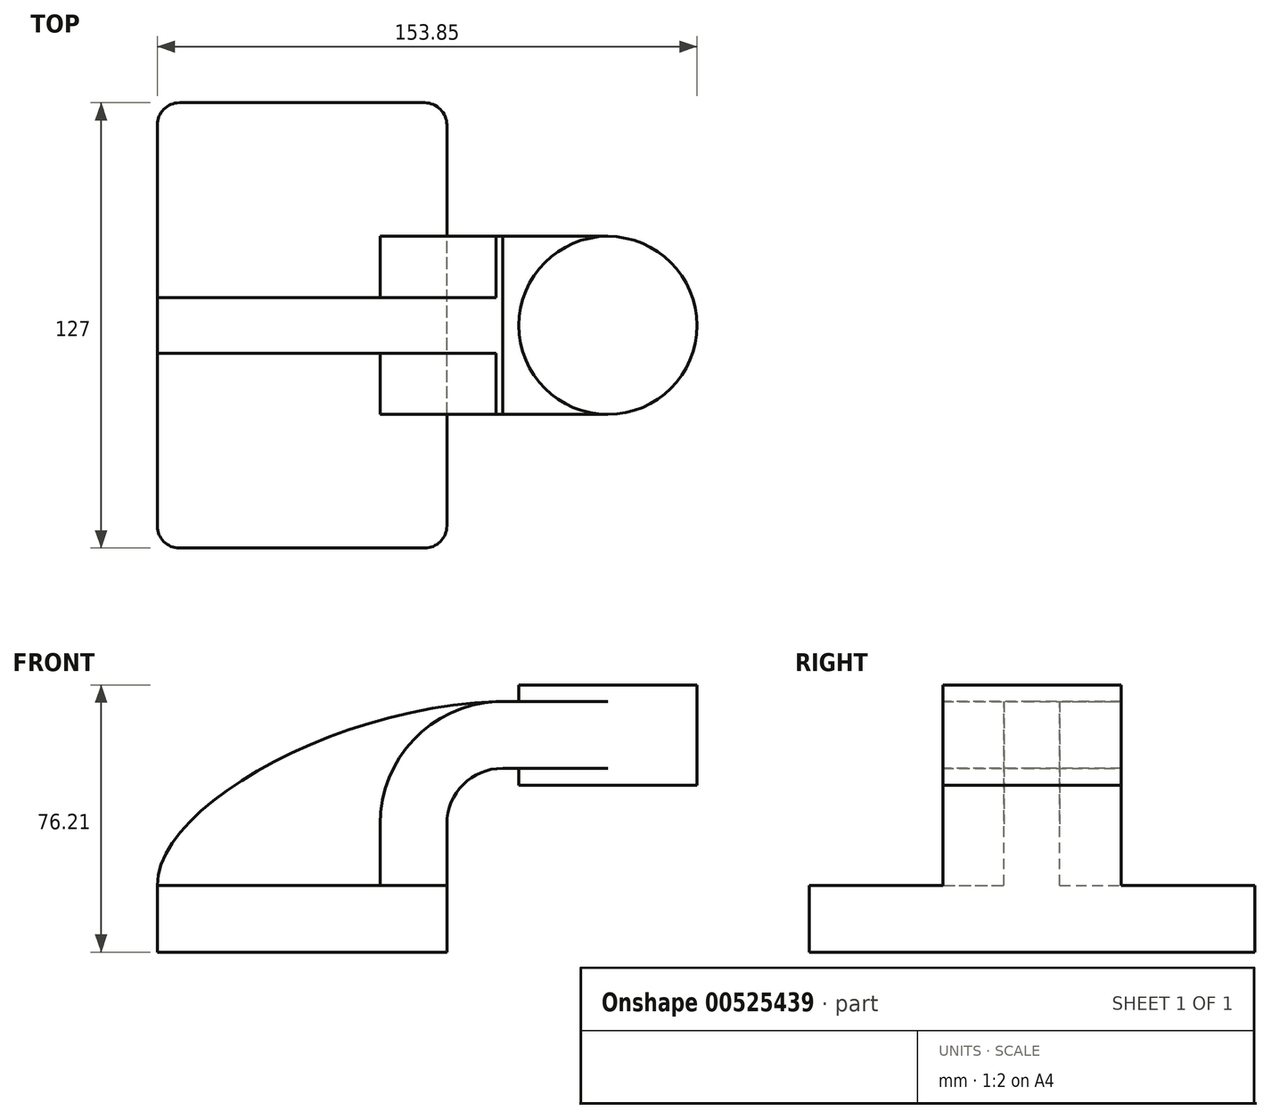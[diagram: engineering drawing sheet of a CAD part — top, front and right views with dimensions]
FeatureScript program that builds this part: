
annotation { "Feature Type Name" : "Feature", "Feature Type Description" : "" }
export const myFeature = defineFeature(function(context is Context, id is Id, definition is map)
    precondition{}
    {
        {
            var Q0;
            Q0=qCreatedBy(makeId("Front.planeOp"),FACE);
            var sketch = newSketch(context, id + "F0", { "sketchPlane" : qUnion([Q0])});
            skLineSegment(sketch, "E0.bottom", {"start": v(-41.28, 9.52) * mm, "end": v(41.27, 9.53) * mm});
            skLineSegment(sketch, "E0.top", {"start": v(-41.28, -9.53) * mm, "end": v(41.28, -9.53) * mm});
            skLineSegment(sketch, "E0.left", {"start": v(-41.28, 9.52) * mm, "end": v(-41.27, -9.53) * mm});
            skLineSegment(sketch, "E0.right", {"start": v(41.28, 9.53) * mm, "end": v(41.28, -9.52) * mm});
            skPoint(sketch, "E0.middle", {"position": v(0, 0) * mm});
            skLineSegment(sketch, "E1.bottom", {"start": v(112.57, 38.1) * mm, "end": v(61.77, 38.1) * mm});
            skLineSegment(sketch, "E1.top", {"start": v(112.57, 66.68) * mm, "end": v(61.77, 66.68) * mm});
            skLineSegment(sketch, "E1.left", {"start": v(112.57, 38.1) * mm, "end": v(112.57, 66.68) * mm});
            skLineSegment(sketch, "E1.right", {"start": v(61.77, 38.1) * mm, "end": v(61.77, 66.68) * mm});
            skPoint(sketch, "E1.middle", {"position": v(87.17, 52.39) * mm});
            skLineSegment(sketch, "E2", {"start": v(41.27, 9.53) * mm, "end": v(41.27, 27) * mm});
            skArc(sketch, "E3", {"start": v(41.27, 27) * mm, "mid": v(45.92, 38.23) * mm, "end": v(57.15, 42.88) * mm});
            skLineSegment(sketch, "E4", {"start": v(57.15, 42.88) * mm, "end": v(87.17, 42.88) * mm});
            skLineSegment(sketch, "E5.0", {"start": v(57.15, 61.93) * mm, "end": v(87.17, 61.93) * mm});
            skArc(sketch, "E5.1", {"start": v(22.22, 27) * mm, "mid": v(32.45, 51.7) * mm, "end": v(57.15, 61.93) * mm});
            skLineSegment(sketch, "E5.2", {"start": v(22.22, 9.53) * mm, "end": v(22.22, 27) * mm});
            skLineSegment(sketch, "E6", {"start": v(87.17, 35.7) * mm, "end": v(87.17, 66.68) * mm});
            skPoint(sketch, "E6.startSnap0", {"position": v(87.17, 38.1) * mm});
            skFitSpline(sketch, "E7", {"points": [v(-41.28, 9.52) * mm, v(57.15, 61.93) * mm], "startDerivative": vector(-0.26, 67.66) * mm, "endDerivative": vector(140.46, 2.62) * mm});
            skSolve(sketch);
        }
        {
            var Q0;
            Q0=makeQuery(id+"F0.imprint","IMPRINT",FACE,{"disambiguationData":[TD([[makeQuery(id+"F0.imprint","IMPRINT",EDGE,{"derivedFrom":sQuery(id+"F0.wireOp",EDGE,"E0.top")}),1.0]])]});
            extrude(context, id + "F1", {"entities" : qUnion([Q0]), "endBound" : BoundingType.SYMMETRIC, "depth" : 127 * mm, "offsetDistance" : 25.4 * mm});
        }
        {
            var Q0;
            {var subQ1=sQuery(id+"F0.wireOp",EDGE,"E2");Q0=makeQuery(id+"F0.imprint","IMPRINT",FACE,{"disambiguationData":[TD([[makeQuery(id+"F0.imprint","IMPRINT",EDGE,{"derivedFrom":subQ1}),1.0]])]});}
            var Q1;
            {var subQ0=sQuery(id+"F0.wireOp",EDGE,"E4");var subQ1=sQuery(id+"F0.wireOp",EDGE,"E1.right");var subQ2=makeQuery(id+"F0.imprint","INTERSECT",VERTEX,{"derivedFrom":[subQ1,subQ0]});Q1=makeQuery(id+"F0.imprint","IMPRINT",FACE,{"disambiguationData":[TD([[makeQuery(id+"F0.imprint","IMPRINT",EDGE,{"disambiguationData":[TD([[subQ2,-1.0]])],"derivedFrom":subQ1}),-1.0]])]});}
            extrude(context, id + "F2", {"entities" : qUnion([Q0, Q1]), "operationType" : NewBodyOperationType.ADD, "endBound" : BoundingType.SYMMETRIC, "depth" : 50.8 * mm, "offsetDistance" : 25.4 * mm});
        }
        {
            var Q0;
            {var subQ3=sQuery(id+"F0.wireOp",EDGE,"E5.2");Q0=makeQuery(id+"F0.imprint","IMPRINT",FACE,{"disambiguationData":[TD([[makeQuery(id+"F0.imprint","IMPRINT",EDGE,{"derivedFrom":subQ3}),1.0]])]});}
            extrude(context, id + "F3", {"entities" : qUnion([Q0]), "operationType" : NewBodyOperationType.ADD, "endBound" : BoundingType.SYMMETRIC, "depth" : 15.88 * mm, "offsetDistance" : 25.4 * mm});
        }
        {
            var Q0;
            {var subQ0=sQuery(id+"F0.wireOp",EDGE,"E1.left");Q0=makeQuery(id+"F0.imprint","IMPRINT",FACE,{"disambiguationData":[TD([[makeQuery(id+"F0.imprint","IMPRINT",EDGE,{"derivedFrom":subQ0}),1.0]])]});}
            var Q1;
            Q1=sQuery(id+"F0.wireOp",EDGE,"E6");
            revolve(context, id + "F4", {"operationType" : NewBodyOperationType.ADD, "entities" : qUnion([Q0]), "axis" : qUnion([Q1]), "revolveType" : RevolveType.FULL});
        }
        {
            var Q0;
            Q0=makeQuery(id+"F1.opExtrude","CAP_EDGE",EDGE,{"disambiguationData":[OSD([sQuery(id+"F0.wireOp",EDGE,"E0.right")])],"isStart":true});
            var Q1;
            Q1=makeQuery(id+"F1.opExtrude","CAP_EDGE",EDGE,{"disambiguationData":[OSD([sQuery(id+"F0.wireOp",EDGE,"E0.left")])],"isStart":true});
            var Q2;
            Q2=makeQuery(id+"F1.opExtrude","CAP_EDGE",EDGE,{"disambiguationData":[OSD([sQuery(id+"F0.wireOp",EDGE,"E0.left")])],"isStart":false});
            var Q3;
            Q3=makeQuery(id+"F1.opExtrude","CAP_EDGE",EDGE,{"disambiguationData":[OSD([sQuery(id+"F0.wireOp",EDGE,"E0.right")])],"isStart":false});
            fillet(context, id + "F5", {"entities" : qUnion([Q0, Q1, Q2, Q3]), "radius" : 6.35 * mm, "tangentPropagation" : true, "allowEdgeOverflow" : false});
        }
    });
